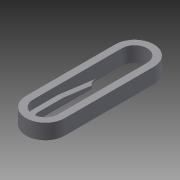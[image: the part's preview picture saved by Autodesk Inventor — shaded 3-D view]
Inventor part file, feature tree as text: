
AUTODESK INVENTOR PART (.ipt)
format: ipt  version: 2015 (Build 190159000, 159)  size: 131,072 bytes
history: native  units: mm
features: sketch x3, extrude x3, plane x1, split x1, boolean_combine x1, other x1
ambient origin geometry x8: Origin, YZ Plane, XZ Plane, XY Plane, X Axis, Y Axis, Z Axis, Center Point
bodies: Solid3 (feature_tree)
feature tree (10):
  sketch  "Sketch6"  dims[d20=3.75mm d21=2.0mm]
  extrude  "Extrusion7"  Depth=2.0mm
  sketch  "Sketch7"  dims[d23=4.5mm d24=4.5mm]
  plane  "Work Plane3"
  extrude  "Extrusion9"  Depth=4.5mm
  split  "Split1"
  boolean_combine  "Combine1"
  extrude  "Extrusion10"  Depth=7.5mm
  other  "Work Axis1"
  sketch  "Sketch8"  dims[d25=0.0mm d28=7.5mm d29=2.0mm d31=2.0mm d32=0.0mm d33=38.0mm d34=0.5mm d35=7.5mm d36=7.5mm d37=10.0mm d38=0.0mm]
